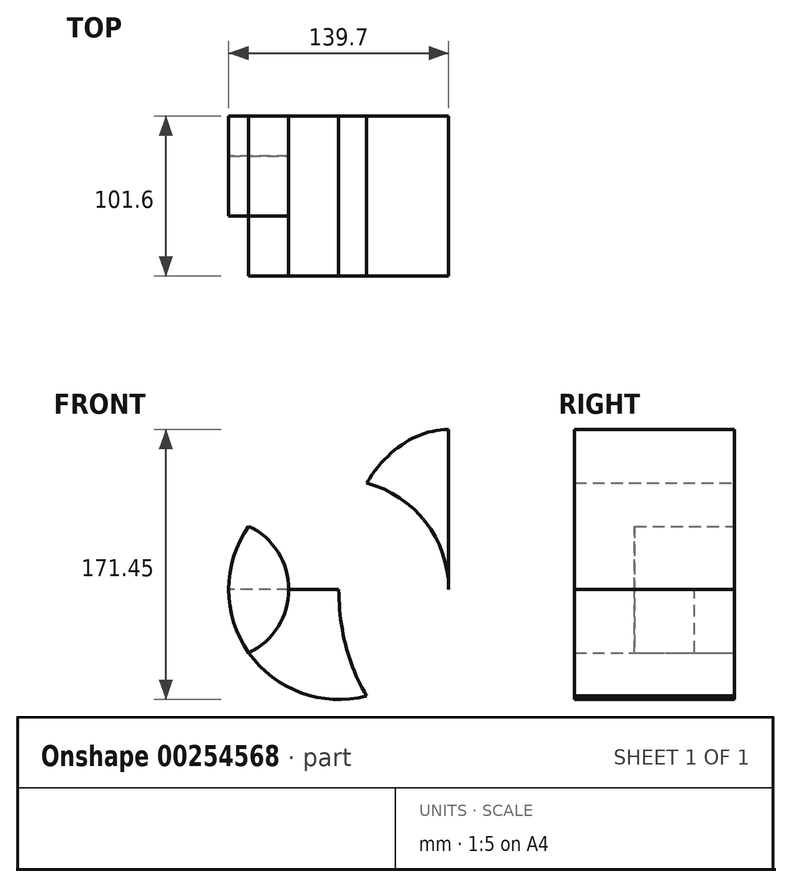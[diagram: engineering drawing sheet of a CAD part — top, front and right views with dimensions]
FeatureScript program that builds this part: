
annotation { "Feature Type Name" : "Feature", "Feature Type Description" : "" }
export const myFeature = defineFeature(function(context is Context, id is Id, definition is map)
    precondition{}
    {
        {
            var Q0;
            Q0=qCreatedBy(makeId("Front.planeOp"),FACE);
            var sketch = newSketch(context, id + "F0", { "sketchPlane" : qUnion([Q0])});
            skLineSegment(sketch, "E0", {"start": v(0, 0) * mm, "end": v(-76.2, 0) * mm});
            skCircle(sketch, "E1", {"center": v(-76.2, 0) * mm, "radius": 44.45 * mm});
            skLineSegment(sketch, "E2", {"start": v(-31.75, 0) * mm, "end": v(-69.85, 0) * mm});
            skCircle(sketch, "E3", {"center": v(0, 0) * mm, "radius": 69.85 * mm});
            skLineSegment(sketch, "E4", {"start": v(69.85, 0) * mm, "end": v(69.74, 101.6) * mm});
            skEllipse(sketch, "E5", {"center": v(69.85, 0) * mm, "majorRadius": 101.6 * mm, "minorRadius": 69.85 * mm, "majorAxis": v(0, 1)});
            skSolve(sketch);
        }
        {
            var Q0;
            {var subQ0=sQuery(id+"F0.wireOp",EDGE,"E3");var subQ1=sQuery(id+"F0.wireOp",EDGE,"E1");var subQ2=makeQuery(id+"F0.imprint","INTERSECT",VERTEX,{"disambiguationData":[OD(0.0)],"derivedFrom":[subQ1,subQ0]});Q0=makeQuery(id+"F0.imprint","IMPRINT",FACE,{"disambiguationData":[TD([[makeQuery(id+"F0.imprint","IMPRINT",EDGE,{"disambiguationData":[TD([[subQ2,-1.0]])],"derivedFrom":subQ1}),1.0]])]});}
            extrude(context, id + "F1", {"entities" : qUnion([Q0]), "depth" : 25.4 * mm});
        }
        {
            var Q0;
            {var subQ3=sQuery(id+"F0.wireOp",EDGE,"E1");var subQ5=sQuery(id+"F0.wireOp",EDGE,"E3");var subQ6=makeQuery(id+"F0.imprint","INTERSECT",VERTEX,{"disambiguationData":[OD(0.0)],"derivedFrom":[subQ3,subQ5]});Q0=makeQuery(id+"F0.imprint","IMPRINT",FACE,{"disambiguationData":[TD([[makeQuery(id+"F0.imprint","IMPRINT",EDGE,{"disambiguationData":[TD([[subQ6,1.0]])],"derivedFrom":subQ5}),1.0]])]});}
            var Q1;
            {var subQ3=sQuery(id+"F0.wireOp",EDGE,"E1");var subQ5=sQuery(id+"F0.wireOp",EDGE,"E3");var subQ6=makeQuery(id+"F0.imprint","INTERSECT",VERTEX,{"disambiguationData":[OD(1.0)],"derivedFrom":[subQ3,subQ5]});Q1=makeQuery(id+"F0.imprint","IMPRINT",FACE,{"disambiguationData":[TD([[makeQuery(id+"F0.imprint","IMPRINT",EDGE,{"disambiguationData":[TD([[subQ6,-1.0]])],"derivedFrom":subQ5}),1.0]])]});}
            var Q2;
            {var subQ0=sQuery(id+"F0.wireOp",EDGE,"E2");Q2=makeQuery(id+"F0.imprint","IMPRINT",FACE,{"disambiguationData":[TD([[makeQuery(id+"F0.imprint","IMPRINT",EDGE,{"derivedFrom":subQ0}),-1.0]])]});}
            var Q3;
            {var subQ0=sQuery(id+"F0.wireOp",EDGE,"E2");Q3=makeQuery(id+"F0.imprint","IMPRINT",FACE,{"disambiguationData":[TD([[makeQuery(id+"F0.imprint","IMPRINT",EDGE,{"derivedFrom":subQ0}),1.0]])]});}
            extrude(context, id + "F2", {"entities" : qUnion([Q0, Q1, Q2, Q3]), "depth" : 63.5 * mm});
        }
        {
            var Q0;
            {var subQ0=sQuery(id+"F0.wireOp",EDGE,"E4");var subQ1=sQuery(id+"F0.wireOp",EDGE,"E3");var subQ2=makeQuery(id+"F0.imprint","INTERSECT",VERTEX,{"disambiguationData":[OD(0.0)],"derivedFrom":[subQ1,subQ0]});Q0=makeQuery(id+"F0.imprint","IMPRINT",FACE,{"disambiguationData":[TD([[makeQuery(id+"F0.imprint","IMPRINT",EDGE,{"disambiguationData":[TD([[subQ2,-1.0]])],"derivedFrom":subQ1}),-1.0]])]});}
            var Q1;
            {var subQ0=sQuery(id+"F0.wireOp",EDGE,"E5");var subQ1=sQuery(id+"F0.wireOp",EDGE,"E3");var subQ2=makeQuery(id+"F0.imprint","INTERSECT",VERTEX,{"disambiguationData":[OD(0.0)],"derivedFrom":[subQ1,subQ0]});Q1=makeQuery(id+"F0.imprint","IMPRINT",FACE,{"disambiguationData":[TD([[makeQuery(id+"F0.imprint","IMPRINT",EDGE,{"disambiguationData":[TD([[subQ2,1.0]])],"derivedFrom":subQ1}),-1.0]])]});}
            var Q2;
            {var subQ0=sQuery(id+"F0.wireOp",EDGE,"E5");var subQ2=sQuery(id+"F0.wireOp",EDGE,"E3");var subQ3=makeQuery(id+"F0.imprint","INTERSECT",VERTEX,{"disambiguationData":[OD(0.0)],"derivedFrom":[subQ2,subQ0]});Q2=makeQuery(id+"F0.imprint","IMPRINT",FACE,{"disambiguationData":[TD([[makeQuery(id+"F0.imprint","IMPRINT",EDGE,{"disambiguationData":[TD([[subQ3,1.0]])],"derivedFrom":subQ2}),1.0]])]});}
            extrude(context, id + "F3", {"entities" : qUnion([Q0, Q1, Q2]), "depth" : 101.6 * mm});
        }
    });
